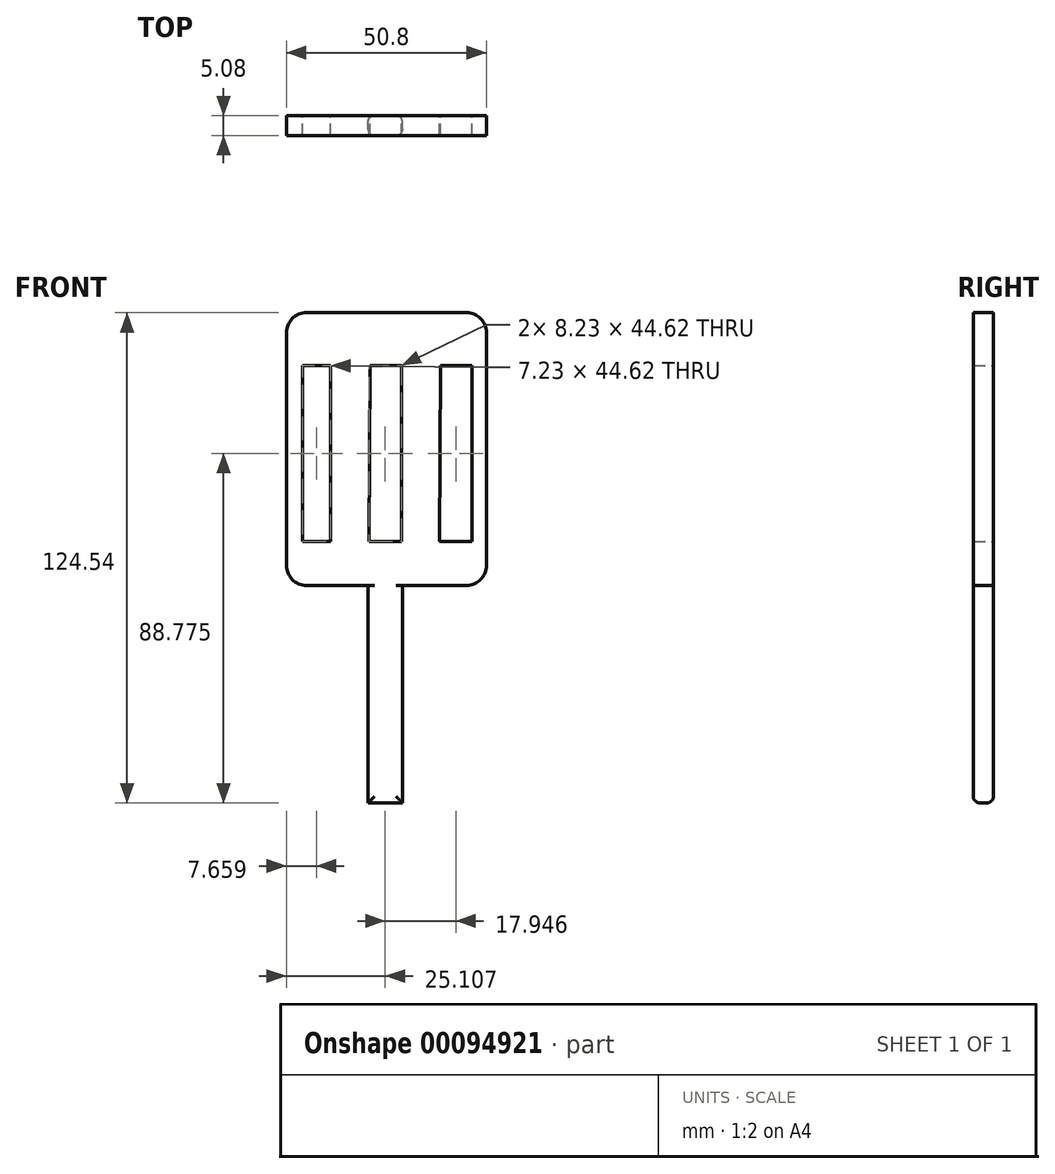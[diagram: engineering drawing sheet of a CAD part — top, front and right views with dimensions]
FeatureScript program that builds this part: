
annotation { "Feature Type Name" : "Feature", "Feature Type Description" : "" }
export const myFeature = defineFeature(function(context is Context, id is Id, definition is map)
    precondition{}
    {
        {
            var Q0;
            Q0=qCreatedBy(makeId("Front.planeOp"),FACE);
            var sketch = newSketch(context, id + "F0", { "sketchPlane" : qUnion([Q0])});
            skLineSegment(sketch, "E0", {"start": v(-25.73, 0) * mm, "end": v(25.07, 0) * mm});
            skLineSegment(sketch, "E1", {"start": v(-4.99, 0) * mm, "end": v(-4.99, -55.24) * mm});
            skLineSegment(sketch, "E2", {"start": v(-4.99, 0) * mm, "end": v(3.74, 0) * mm});
            skLineSegment(sketch, "E3", {"start": v(3.74, 0) * mm, "end": v(3.74, -55.24) * mm});
            skLineSegment(sketch, "E4", {"start": v(3.74, -55.24) * mm, "end": v(-4.99, -55.24) * mm});
            skLineSegment(sketch, "E5", {"start": v(-25.73, 69.3) * mm, "end": v(25.07, 69.3) * mm});
            skLineSegment(sketch, "E6", {"start": v(-25.73, 69.3) * mm, "end": v(-25.73, 0) * mm});
            skLineSegment(sketch, "E7", {"start": v(25.07, 69.3) * mm, "end": v(25.07, 0) * mm});
            skLineSegment(sketch, "E8", {"start": v(-21.68, 51.84) * mm, "end": v(-21.68, 55.83) * mm});
            skLineSegment(sketch, "E9", {"start": v(-14.46, 55.83) * mm, "end": v(-14.46, 11.22) * mm});
            skLineSegment(sketch, "E10", {"start": v(-14.46, 11.22) * mm, "end": v(-21.68, 11.22) * mm});
            skLineSegment(sketch, "E11", {"start": v(-14.46, 55.83) * mm, "end": v(-21.68, 55.83) * mm});
            skLineSegment(sketch, "E12", {"start": v(-4.49, 55.83) * mm, "end": v(3.49, 55.83) * mm});
            skLineSegment(sketch, "E13", {"start": v(3.49, 55.83) * mm, "end": v(3.49, 11.22) * mm});
            skLineSegment(sketch, "E14", {"start": v(3.49, 11.22) * mm, "end": v(-4.74, 11.22) * mm});
            skLineSegment(sketch, "E15", {"start": v(-4.49, 55.83) * mm, "end": v(-4.74, 11.22) * mm});
            skLineSegment(sketch, "E16", {"start": v(13.46, 55.83) * mm, "end": v(21.44, 55.83) * mm});
            skLineSegment(sketch, "E17", {"start": v(21.44, 55.83) * mm, "end": v(21.44, 11.22) * mm});
            skLineSegment(sketch, "E18", {"start": v(21.44, 11.22) * mm, "end": v(13.21, 11.22) * mm});
            skLineSegment(sketch, "E19", {"start": v(13.21, 11.22) * mm, "end": v(13.46, 55.83) * mm});
            skLineSegment(sketch, "E20", {"start": v(-21.68, 55.83) * mm, "end": v(-21.68, 11.22) * mm});
            skSolve(sketch);
        }
        {
            var Q0;
            Q0 = qSketchRegion(id + "F0", true);
            extrude(context, id + "F1", {"entities" : qUnion([Q0]), "depth" : 5.08 * mm});
        }
        {
            var Q0;
            Q0=makeQuery(id+"F1.opExtrude","SWEPT_EDGE",EDGE,{"disambiguationData":[OSD([sQuery(id+"F0.wireOp",EDGE,"E5"),sQuery(id+"F0.wireOp",EDGE,"E6")])]});
            var Q1;
            Q1=makeQuery(id+"F1.opExtrude","SWEPT_EDGE",EDGE,{"disambiguationData":[OSD([sQuery(id+"F0.wireOp",EDGE,"E5"),sQuery(id+"F0.wireOp",EDGE,"E7")])]});
            fillet(context, id + "F2", {"entities" : qUnion([Q0, Q1]), "radius" : 5.08 * mm, "tangentPropagation" : true, "allowEdgeOverflow" : false});
        }
        {
            var Q0;
            Q0=makeQuery(id+"F1.opExtrude","SWEPT_EDGE",EDGE,{"disambiguationData":[OSD([sQuery(id+"F0.wireOp",EDGE,"E0"),sQuery(id+"F0.wireOp",EDGE,"E6")])]});
            var Q1;
            Q1=makeQuery(id+"F1.opExtrude","SWEPT_EDGE",EDGE,{"disambiguationData":[OSD([sQuery(id+"F0.wireOp",EDGE,"E0"),sQuery(id+"F0.wireOp",EDGE,"E7")])]});
            fillet(context, id + "F3", {"entities" : qUnion([Q0, Q1]), "radius" : 5.08 * mm, "tangentPropagation" : true, "allowEdgeOverflow" : false});
        }
        {
            var Q0;
            Q0=makeQuery(id+"F1.opExtrude","CAP_EDGE",EDGE,{"disambiguationData":[OSD([sQuery(id+"F0.wireOp",EDGE,"E3")])],"isStart":true});
            var Q1;
            Q1=makeQuery(id+"F1.opExtrude","CAP_EDGE",EDGE,{"disambiguationData":[OSD([sQuery(id+"F0.wireOp",EDGE,"E4")])],"isStart":true});
            var Q2;
            Q2=makeQuery(id+"F1.opExtrude","CAP_EDGE",EDGE,{"disambiguationData":[OSD([sQuery(id+"F0.wireOp",EDGE,"E1")])],"isStart":true});
            var Q3;
            Q3=makeQuery(id+"F1.opExtrude","CAP_EDGE",EDGE,{"disambiguationData":[OSD([sQuery(id+"F0.wireOp",EDGE,"E3")])],"isStart":false});
            var Q4;
            Q4=makeQuery(id+"F1.opExtrude","CAP_EDGE",EDGE,{"disambiguationData":[OSD([sQuery(id+"F0.wireOp",EDGE,"E1")])],"isStart":false});
            var Q5;
            Q5=makeQuery(id+"F1.opExtrude","CAP_EDGE",EDGE,{"disambiguationData":[OSD([sQuery(id+"F0.wireOp",EDGE,"E4")])],"isStart":false});
            fillet(context, id + "F4", {"entities" : qUnion([Q0, Q1, Q2, Q3, Q4, Q5]), "radius" : 1.59 * mm, "tangentPropagation" : true, "allowEdgeOverflow" : false});
        }
    });
